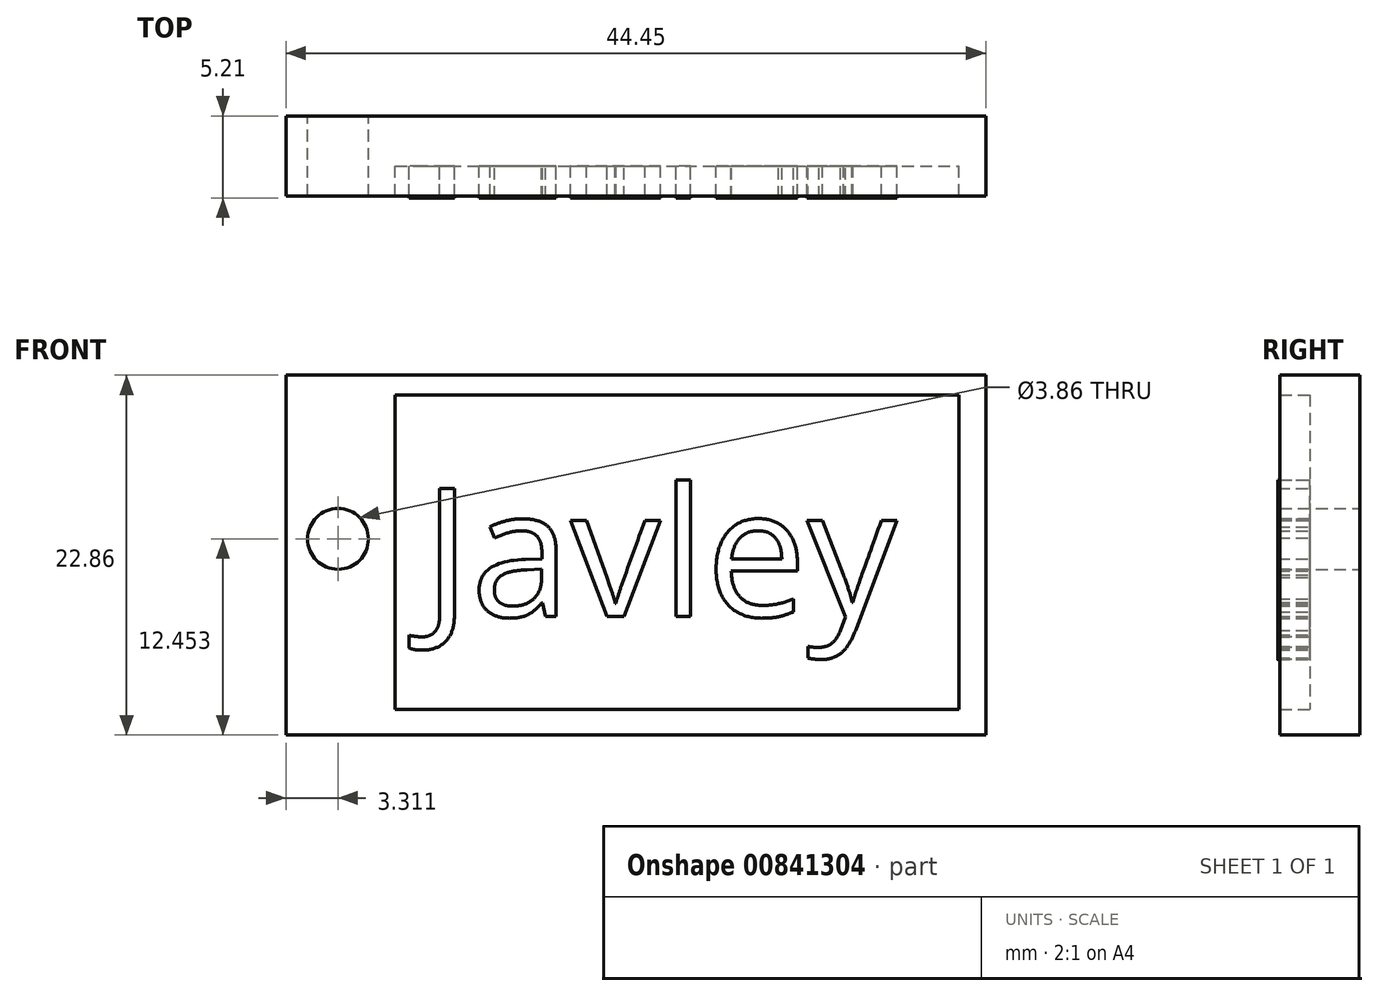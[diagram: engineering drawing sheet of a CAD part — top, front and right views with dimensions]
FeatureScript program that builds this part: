
annotation { "Feature Type Name" : "Feature", "Feature Type Description" : "" }
export const myFeature = defineFeature(function(context is Context, id is Id, definition is map)
    precondition{}
    {
        {
            var Q0;
            Q0=qCreatedBy(makeId("Front.planeOp"),FACE);
            var sketch = newSketch(context, id + "F0", { "sketchPlane" : qUnion([Q0])});
            skLineSegment(sketch, "E0", {"start": v(0, 0) * mm, "end": v(0, 22.86) * mm});
            skLineSegment(sketch, "E1", {"start": v(0, 22.86) * mm, "end": v(44.45, 22.86) * mm});
            skLineSegment(sketch, "E2", {"start": v(44.45, 22.86) * mm, "end": v(44.45, 0) * mm});
            skLineSegment(sketch, "E3", {"start": v(44.45, 0) * mm, "end": v(0, 0) * mm});
            skCircle(sketch, "E4", {"center": v(3.31, 12.45) * mm, "radius": 1.93 * mm});
            skLineSegment(sketch, "E5.bottom", {"start": v(6.94, 21.6) * mm, "end": v(42.75, 21.6) * mm});
            skLineSegment(sketch, "E5.top", {"start": v(6.94, 1.64) * mm, "end": v(42.75, 1.64) * mm});
            skLineSegment(sketch, "E5.left", {"start": v(6.94, 21.6) * mm, "end": v(6.94, 1.64) * mm});
            skLineSegment(sketch, "E5.right", {"start": v(42.75, 21.6) * mm, "end": v(42.75, 1.64) * mm});
            skSolve(sketch);
        }
        {
            var Q0;
            Q0 = qSketchRegion(id + "F0", true);
            extrude(context, id + "F1", {"entities" : qUnion([Q0]), "depth" : 5.08 * mm, "offsetDistance" : 25.4 * mm});
        }
        {
            var Q0;
            Q0=makeQuery(id+"F0.imprint","IMPRINT",FACE,{"disambiguationData":[TD([[makeQuery(id+"F0.imprint","IMPRINT",EDGE,{"derivedFrom":sQuery(id+"F0.wireOp",EDGE,"E5.bottom")}),-1.0]])]});
            extrude(context, id + "F2", {"entities" : qUnion([Q0]), "operationType" : NewBodyOperationType.ADD, "depth" : 3.17 * mm, "offsetDistance" : 25.4 * mm});
        }
        {
            var Q0;
            Q0=makeQuery(id+"F2.opExtrude","CAP_FACE",FACE,{"disambiguationData":[OSD([sQuery(id+"F0.wireOp",EDGE,"E5.bottom"),sQuery(id+"F0.wireOp",EDGE,"E5.top"),sQuery(id+"F0.wireOp",EDGE,"E5.left"),sQuery(id+"F0.wireOp",EDGE,"E5.right")])],"isStart":false});
            var sketch = newSketch(context, id + "F3", { "sketchPlane" : qUnion([Q0])});
            skText(sketch, "E6", { "text": "Javley\n", "fontName": "OpenSans-Regular.ttf"});
            const initialGuessF3  = {"E6": [0.0087, 0.00753, 1, 0, 0.00821]};
            skSetInitialGuess(sketch, initialGuessF3);
            skSolve(sketch);
        }
        {
            var Q0;
            Q0 = qSketchRegion(id + "F3", true);
            extrude(context, id + "F4", {"entities" : qUnion([Q0]), "operationType" : NewBodyOperationType.ADD, "depth" : 2.03 * mm, "offsetDistance" : 25.4 * mm});
        }
    });
